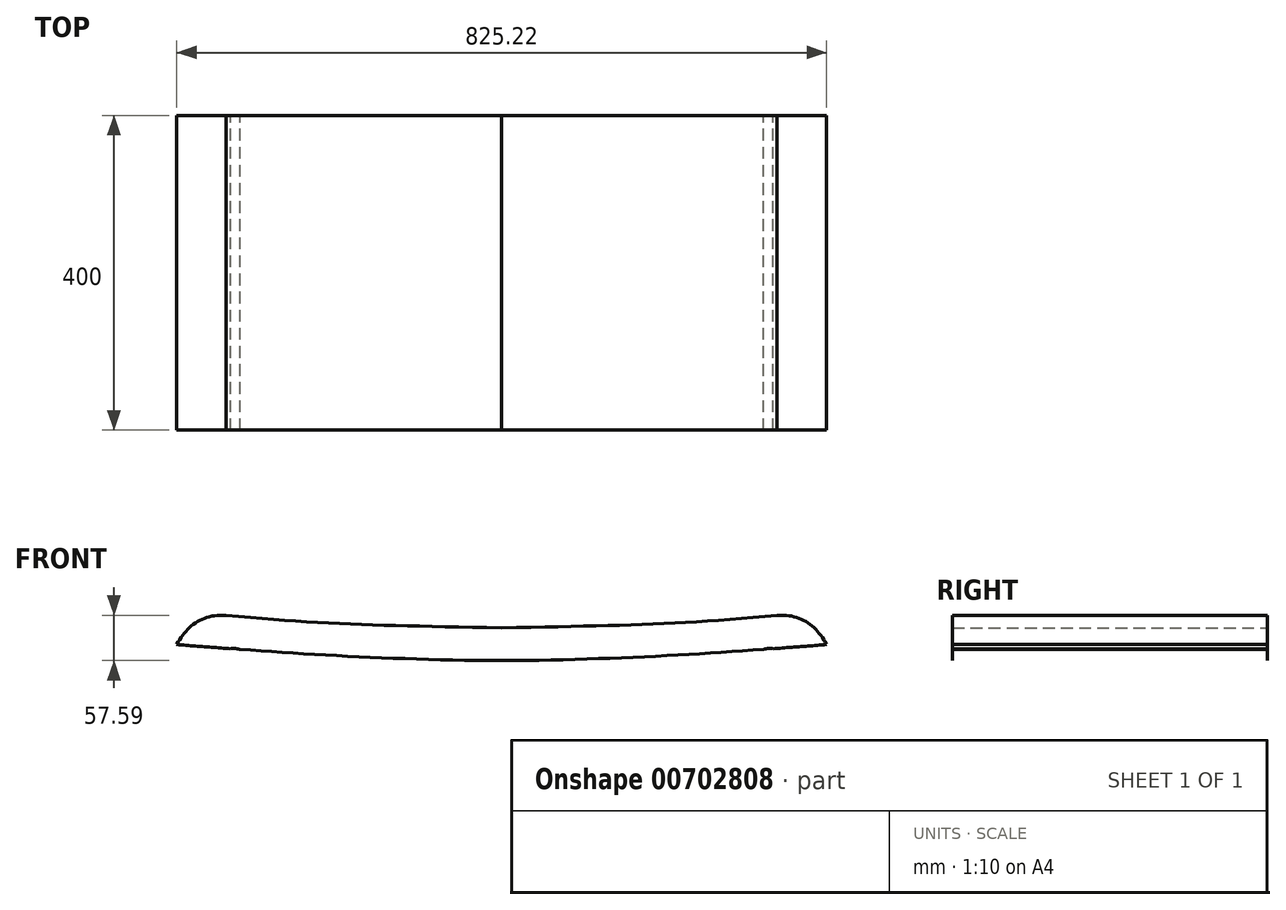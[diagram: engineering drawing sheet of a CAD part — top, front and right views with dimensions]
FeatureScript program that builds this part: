
annotation { "Feature Type Name" : "Feature", "Feature Type Description" : "" }
export const myFeature = defineFeature(function(context is Context, id is Id, definition is map)
    precondition{}
    {
        {
            var Q0;
            Q0=qCreatedBy(makeId("Front.planeOp"),FACE);
            var sketch = newSketch(context, id + "F0", { "sketchPlane" : qUnion([Q0])});
            skPoint(sketch, "E0.middle", {"position": v(0, 0) * mm});
            skFitSpline(sketch, "E1", {"points": [v(-368.19, 166.53) * mm, v(0, 148.77) * mm], "startDerivative": vector(395.1, -40.66) * mm, "endDerivative": vector(467.3, -9.46) * mm});
            skFitSpline(sketch, "E2", {"points": [v(-350, 164.7) * mm, v(-350, -215.32) * mm], "startDerivative": vector(-392.06, 24.79) * mm, "endDerivative": vector(233.27, -240.17) * mm});
            skFitSpline(sketch, "E3", {"points": [v(-350, -215.32) * mm, v(0, -119) * mm], "startDerivative": vector(187.36, -199.58) * mm, "endDerivative": vector(467.3, -0.51) * mm});
            skLineSegment(sketch, "E4", {"start": v(0, 107.27) * mm, "end": v(0, -86.47) * mm});
            skFitSpline(sketch, "E5", {"points": [v(-462.34, 131.3) * mm, v(0, 107.27) * mm], "startDerivative": vector(411.22, -31.21) * mm, "endDerivative": vector(529.39, -2.03) * mm});
            skFitSpline(sketch, "E6", {"points": [v(-332.26, 121.42) * mm, v(-316.56, -177.24) * mm], "startDerivative": vector(-217.16, 58.54) * mm, "endDerivative": vector(277.95, -261.17) * mm});
            skFitSpline(sketch, "E7", {"points": [v(-316.56, -177.24) * mm, v(0, -86.47) * mm], "startDerivative": vector(81.3, -96.05) * mm, "endDerivative": vector(523.85, -8.77) * mm});
            skFitSpline(sketch, "E8.MirrorCS", {"points": [v(368.19, 166.53) * mm, v(0, 148.77) * mm], "startDerivative": vector(-395.1, -40.66) * mm, "endDerivative": vector(-467.3, -9.46) * mm});
            skFitSpline(sketch, "E9.MirrorCS", {"points": [v(462.34, 131.3) * mm, v(0, 107.27) * mm], "startDerivative": vector(-411.22, -31.21) * mm, "endDerivative": vector(-529.39, -2.03) * mm});
            skFitSpline(sketch, "E10.MirrorCS", {"points": [v(350, 164.7) * mm, v(350, -215.32) * mm], "startDerivative": vector(392.06, 24.79) * mm, "endDerivative": vector(-233.27, -240.17) * mm});
            skFitSpline(sketch, "E11.MirrorCS", {"points": [v(332.26, 121.42) * mm, v(316.56, -177.24) * mm], "startDerivative": vector(217.16, 58.54) * mm, "endDerivative": vector(-277.95, -261.17) * mm});
            skFitSpline(sketch, "E12.MirrorCS", {"points": [v(350, -215.32) * mm, v(0, -119) * mm], "startDerivative": vector(-187.36, -199.58) * mm, "endDerivative": vector(-467.3, -0.51) * mm});
            skFitSpline(sketch, "E13.MirrorCS", {"points": [v(316.56, -177.24) * mm, v(0, -86.47) * mm], "startDerivative": vector(-81.3, -96.05) * mm, "endDerivative": vector(-523.85, -8.77) * mm});
            skSolve(sketch);
        }
        {
            var Q0;
            Q0=makeQuery(id+"F0.imprint","IMPRINT",FACE,{"disambiguationData":[TD([[makeQuery(id+"F0.imprint","IMPRINT",EDGE,{"derivedFrom":sQuery(id+"F0.wireOp",EDGE,"E1")}),-1.0]])]});
            extrude(context, id + "F1", {"entities" : qUnion([Q0]), "depth" : 400 * mm, "offsetDistance" : 25 * mm});
        }
    });
